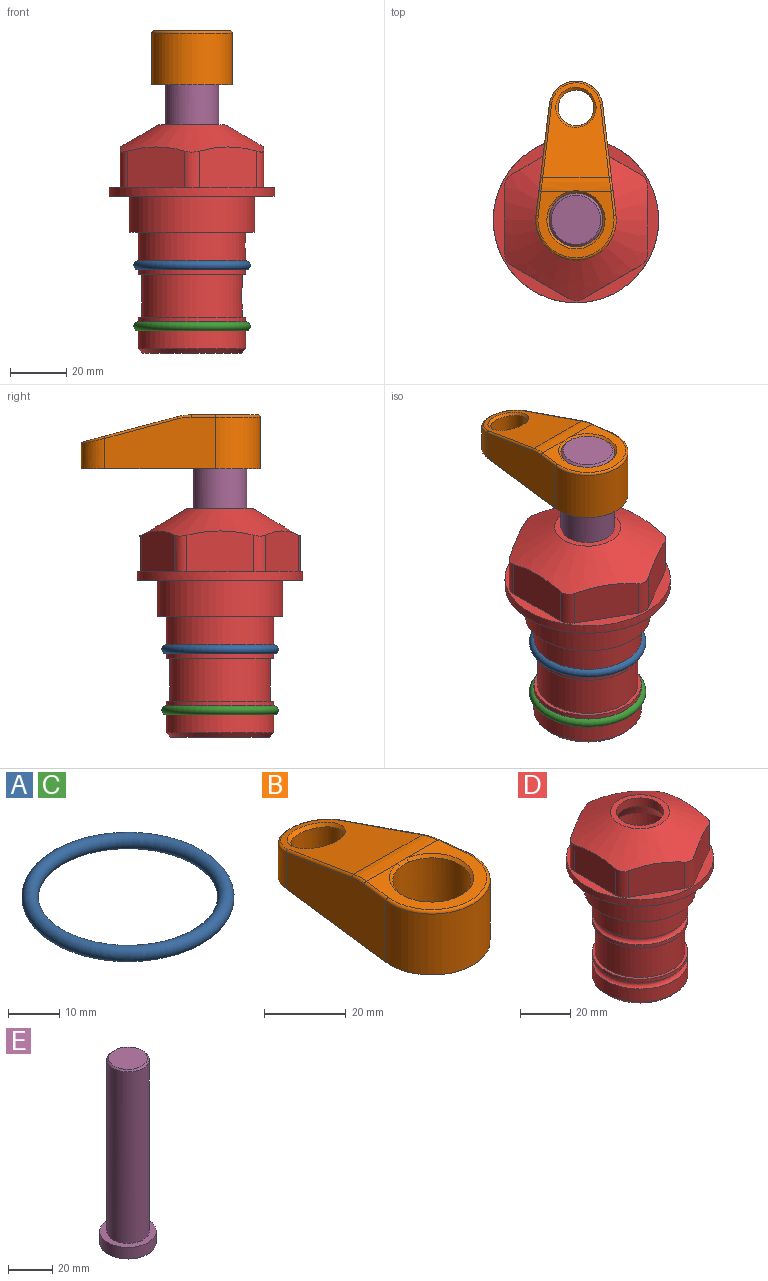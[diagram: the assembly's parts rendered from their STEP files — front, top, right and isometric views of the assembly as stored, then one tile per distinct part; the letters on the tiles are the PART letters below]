
ASSEMBLY  parts=5 mates=4
PART A: 1 faces, bbox 44.7x44.7x3.2 mm
  f0: torus R=19.05mm, axis (0,0,1), area 1193.9mm2
PART B: 31 faces, bbox 31.7x65.5x19.8 mm
  f0: plane 39.12x18.26mm, normal (0.99,0.12,0), area 612.2mm2, adj f1,f4,f7,f11,f13,f15
  f1: cylinder r=9.53mm len=18.91mm, axis (0,0,-1), area 296.1mm2, adj f0,f2,f7,f17
  f2: plane 39.12x18.26mm, normal (-0.99,0.12,0), area 612.2mm2, adj f1,f4,f7,f12,f14,f16
  f3: cylinder r=6.35mm len=12.7mm, axis (0,0,-1), area 362.4mm2, adj f7,f18
  f4: cylinder r=14.29mm len=28.58mm, axis (0,0,-1), area 882.2mm2, adj f0,f2,f7,f10
  f5: cylinder r=9.53mm len=19.05mm, axis (0,0,-1), area 1092.6mm2, adj f7,f19,f20
  f6: plane 26.99x23.69mm, normal (0,0,1), area 216.2mm2, adj f9,f10,f11,f12,f19
  f7: plane 63.5x28.58mm, normal (0,0,-1), area 661.8mm2, adj f0,f1,f2,f3,f4,f5,f22,f23
  f8: plane 33.52x23.6mm, normal (0,0.26,0.97), area 486mm2, adj f9,f15,f16,f17,f18
  f9: cylinder r=19.05mm len=24.72mm, axis (1,0,0), area 120.4mm2, adj f6,f8,f13,f14,f20
  f10: torus R=13.49mm, axis (0,0,1), area 59mm2, adj f4,f6,f11,f12
  f11: cylinder r=0.79mm len=8.67mm, axis (0.12,-0.99,0), area 10.8mm2, adj f0,f6,f10,f13
  f12: cylinder r=0.79mm len=8.67mm, axis (0.12,0.99,0), area 10.8mm2, adj f2,f6,f10,f14
  f13: bspline ~4.95x1.42mm, area 6.1mm2, adj f0,f9,f11,f15
  f14: bspline ~4.95x1.42mm, area 6.1mm2, adj f2,f9,f12,f16
  f15: cylinder r=0.79mm len=25.95mm, axis (0.12,-0.96,0.26), area 32.9mm2, adj f0,f8,f13,f17
  f16: cylinder r=0.79mm len=25.95mm, axis (0.12,0.96,-0.26), area 32.9mm2, adj f2,f8,f14,f17
  f17: bspline ~18.91x8.38mm, area 30mm2, adj f1,f8,f15,f16
  f18: bspline ~14.29x14.29mm, area 48.3mm2, adj f3,f8
  f19: cone r=9.53mm half-angle=45deg, axis (0,0,1), area 66.5mm2, adj f5,f6,f20
  f20: bspline ~3.22x0.96mm, area 3.5mm2, adj f5,f9,f19
  f21: plane 2.75x2.72mm, normal (0,0,-1), area 2.9mm2, adj f23,f25,f28
  f22: plane 23.05x15.88mm, normal (-0.99,-0.12,0), area 323.6mm2, adj f7,f25,f26,f27,f28,f29
  f23: plane 23.05x15.88mm, normal (0.99,-0.12,0), area 323.6mm2, adj f7,f21,f25,f27,f28,f30
  f24: cylinder r=9.53mm len=10.69mm, axis (0,0,-1), area 114.7mm2, adj f7,f27,f29,f30
  f25: cylinder r=12.7mm len=20.59mm, axis (0,0,-1), area 381.1mm2, adj f7,f21,f22,f23,f26,f28
  f26: plane 2.75x2.72mm, normal (0,0,-1), area 2.9mm2, adj f22,f25,f28
  f27: plane 19.72x18.37mm, normal (0,-0.26,-0.97), area 291.8mm2, adj f22,f23,f24,f28,f29,f30
  f28: cylinder r=15.88mm len=19.92mm, axis (1,0,0), area 54.8mm2, adj f21,f22,f23,f25,f26,f27
  f29: cylinder r=1.59mm len=11mm, axis (0,0,-1), area 34.7mm2, adj f7,f22,f24,f27
  f30: cylinder r=1.59mm len=11mm, axis (0,0,-1), area 34.7mm2, adj f7,f23,f24,f27
PART C: same geometry as A
PART D: 36 faces, bbox 58.7x58.7x81 mm
  f0: cylinder r=17.78mm len=35.56mm, axis (0,0,1), area 1670.8mm2, adj f23,f24,f31
  f1: cylinder r=19.05mm len=38.1mm, axis (0,0,1), area 1191.9mm2, adj f26,f27,f30
  f2: plane 58.66x58.66mm, normal (0,0,-1), area 1150.6mm2, adj f3,f28
  f3: cylinder r=29.33mm len=58.66mm, axis (0,0,-1), area 585.1mm2, adj f2,f4
  f4: plane 58.66x58.66mm, normal (0,0,1), area 475.9mm2, adj f3,f5,f6,f7,f8,f9,f10,f11
  f5: plane 20.32x14.34mm, normal (-0.5,0.87,0), area 324.4mm2, adj f4,f15,f16,f17
  f6: plane 20.32x14.34mm, normal (0.5,0.87,0), area 324.4mm2, adj f4,f14,f15,f17
  f7: plane 23.48x14.34mm, normal (1,0,0), area 324.4mm2, adj f4,f13,f14,f17
  f8: plane 20.32x14.34mm, normal (0.5,-0.87,0), area 324.4mm2, adj f4,f12,f13,f17
  f9: plane 20.32x14.34mm, normal (-0.5,-0.87,0), area 324.4mm2, adj f4,f11,f12,f17
  f10: plane 23.48x14.34mm, normal (-1,0,0), area 324.4mm2, adj f4,f11,f16,f17
  f11: cylinder r=5.08mm len=12.85mm, axis (0,0,-1), area 67.2mm2, adj f4,f9,f10,f17
  f12: cylinder r=5.08mm len=12.85mm, axis (0,0,-1), area 67.2mm2, adj f4,f8,f9,f17
  f13: cylinder r=5.08mm len=12.85mm, axis (0,0,-1), area 67.2mm2, adj f4,f7,f8,f17
  f14: cylinder r=5.08mm len=12.85mm, axis (0,0,-1), area 67.2mm2, adj f4,f6,f7,f17
  f15: cylinder r=5.08mm len=12.85mm, axis (0,0,-1), area 67.2mm2, adj f4,f5,f6,f17
  f16: cylinder r=5.08mm len=12.85mm, axis (0,0,-1), area 67.2mm2, adj f4,f5,f10,f17
  f17: cone r=11.73mm half-angle=60deg, axis (0,0,-1), area 2071.8mm2, adj f5,f6,f7,f8,f9,f10,f11,f12
  f18: plane 23.46x23.46mm, normal (0,0,1), area 147.4mm2, adj f17,f35
  f19: plane 34.93x34.93mm, normal (0,0,-1), area 958mm2, adj f29
  f20: cylinder r=19.05mm len=38.1mm, axis (0,0,1), area 760.1mm2, adj f21,f29
  f21: torus R=19.05mm, axis (0,0,1), area 565.3mm2, adj f20,f22
  f22: cylinder r=19.05mm len=38.1mm, axis (0,0,1), area 190mm2, adj f21,f23
  f23: plane 38.1x38.1mm, normal (0,0,1), area 146.9mm2, adj f0,f22
  f24: plane 38.1x38.1mm, normal (0,0,-1), area 146.9mm2, adj f0,f25
  f25: cylinder r=19.05mm len=38.1mm, axis (0,0,1), area 190mm2, adj f24,f26
  f26: torus R=19.05mm, axis (0,0,1), area 565.3mm2, adj f1,f25
  f27: plane 44.45x44.45mm, normal (0,0,-1), area 411.7mm2, adj f1,f28
  f28: cylinder r=22.23mm len=44.45mm, axis (0,0,1), area 1773.5mm2, adj f2,f27
  f29: cone r=19.05mm half-angle=45deg, axis (0,0,1), area 257.5mm2, adj f19,f20
  f30: cylinder r=3.17mm len=6.75mm, axis (-1,0,0), area 128mm2, adj f1,f33
  f31: cylinder r=3.17mm len=6.35mm, axis (-1,0,0), area 102.5mm2, adj f0,f33
  f32: plane 25.4x25.4mm, normal (0,0,1), area 506.7mm2, adj f33
  f33: cylinder r=12.7mm len=66.42mm, axis (0,0,-1), area 5236.2mm2, adj f30,f31,f32,f34
  f34: cone r=9.53mm half-angle=30deg, axis (0,0,-1), area 443.4mm2, adj f33,f35
  f35: cylinder r=9.53mm len=19.05mm, axis (0,0,-1), area 240.9mm2, adj f18,f34
PART E: 6 faces, bbox 25.4x25.4x101.6 mm
  f0: plane 17.46x17.46mm, normal (0,0,1), area 239.5mm2, adj f5
  f1: plane 25.4x25.4mm, normal (0,0,-1), area 506.7mm2, adj f2
  f2: cylinder r=12.7mm len=25.4mm, axis (0,0,1), area 506.7mm2, adj f1,f3
  f3: plane 25.4x25.4mm, normal (0,0,1), area 221.7mm2, adj f2,f4
  f4: cylinder r=9.53mm len=94.46mm, axis (0,0,1), area 5653mm2, adj f3,f5
  f5: cone r=8.73mm half-angle=45deg, axis (0,0,-1), area 64.4mm2, adj f0,f4
PLACE A at identity
PLACE B t=(0,0,-4.83)mm
PLACE C t=(0,0,-21.59)mm
PLACE D at identity fixed
PLACE E t=(0,0,-4.83)mm
MATE cylindrical E.f2 <-> D.f0  axis (0,0,-1) through (0,0,-42.93)mm
MATE fastened C.f0 <-> D.f0  axis (0,0,1) through (0,0,-46.1)mm
MATE fastened E.f2 <-> B.f4  axis (0,0,1) through (0,0,58.67)mm
MATE fastened A.f0 <-> D.f0  axis (0,0,1) through (0,0,-24.51)mm
